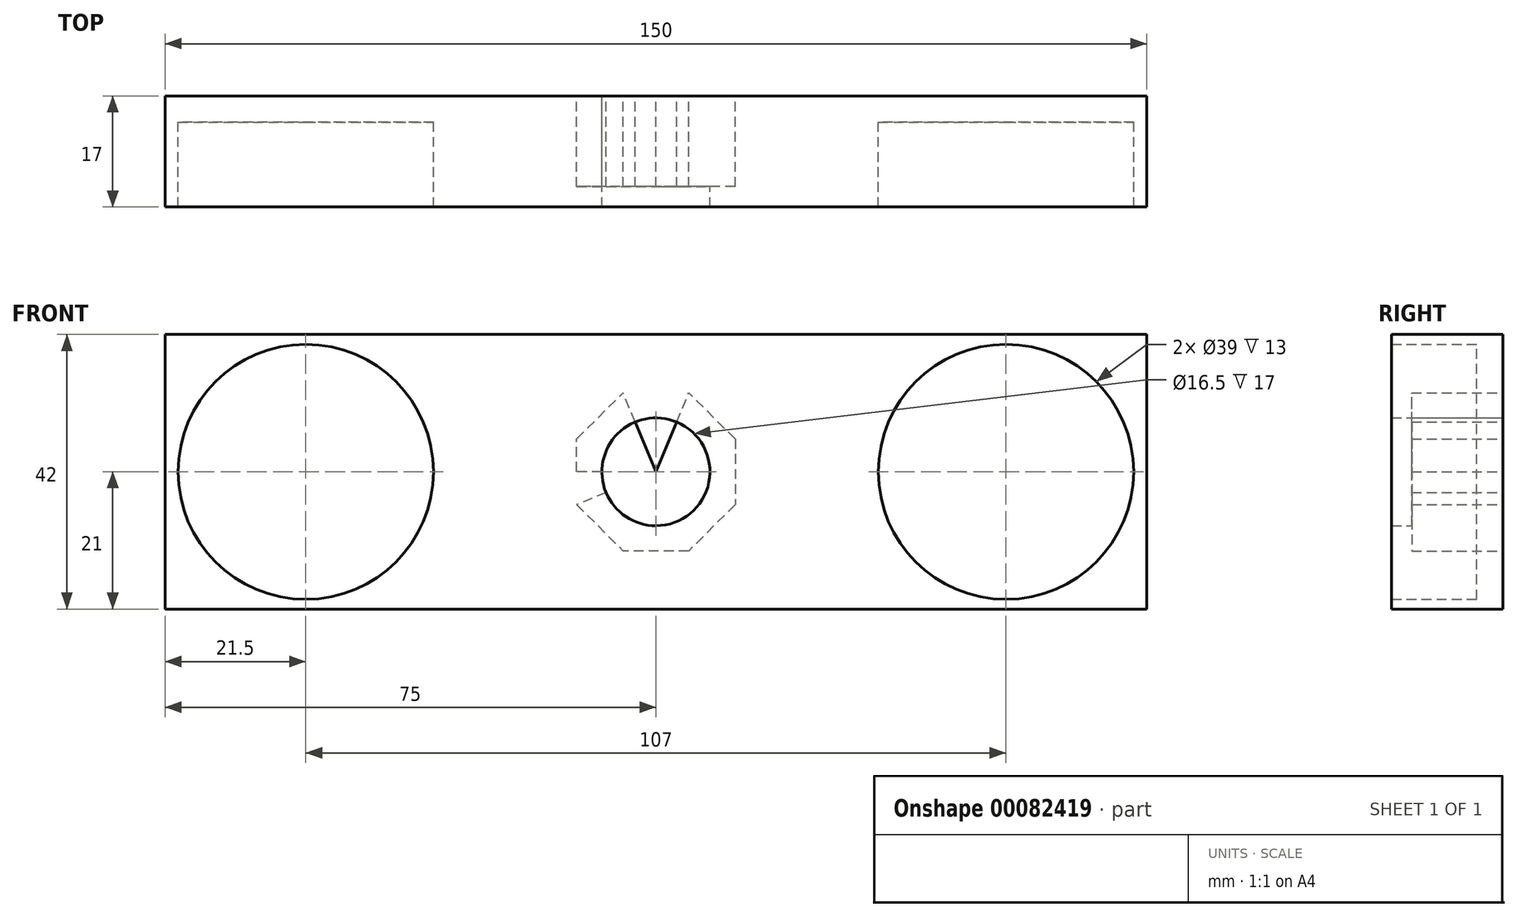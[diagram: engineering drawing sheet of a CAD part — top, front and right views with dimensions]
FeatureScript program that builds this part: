
annotation { "Feature Type Name" : "Feature", "Feature Type Description" : "" }
export const myFeature = defineFeature(function(context is Context, id is Id, definition is map)
    precondition{}
    {
        {
            var Q0;
            Q0=qCreatedBy(makeId("Front.planeOp"),FACE);
            var sketch = newSketch(context, id + "F0", { "sketchPlane" : qUnion([Q0])});
            skLineSegment(sketch, "E0", {"start": v(0, 0) * mm, "end": v(0, 12.1) * mm});
            skLineSegment(sketch, "E1", {"start": v(0, 0) * mm, "end": v(0, -12.1) * mm});
            skLineSegment(sketch, "E2", {"start": v(0, 0) * mm, "end": v(-12.1, 0) * mm});
            skLineSegment(sketch, "E3", {"start": v(0, 0) * mm, "end": v(12.1, 0) * mm});
            skLineSegment(sketch, "E4", {"start": v(0, 12.1) * mm, "end": v(-36.9, 12.1) * mm});
            skLineSegment(sketch, "E5", {"start": v(0, 12.1) * mm, "end": v(53.23, 12.1) * mm});
            skLineSegment(sketch, "E6", {"start": v(0, 0) * mm, "end": v(-5.01, 12.1) * mm});
            skLineSegment(sketch, "E7", {"start": v(0, 0) * mm, "end": v(5.01, 12.1) * mm});
            skLineSegment(sketch, "E8", {"start": v(-5.01, 12.1) * mm, "end": v(5.01, 12.1) * mm});
            skLineSegment(sketch, "E9", {"start": v(-12.1, 0) * mm, "end": v(-12.1, 10.02) * mm});
            skLineSegment(sketch, "E10", {"start": v(-12.1, 0) * mm, "end": v(-12.1, -15.45) * mm});
            skLineSegment(sketch, "E11", {"start": v(0, -12.1) * mm, "end": v(-25.46, -12.1) * mm});
            skLineSegment(sketch, "E12", {"start": v(0, -12.1) * mm, "end": v(28.03, -12.1) * mm});
            skLineSegment(sketch, "E13", {"start": v(12.1, 0) * mm, "end": v(12.1, 12.1) * mm});
            skLineSegment(sketch, "E14", {"start": v(12.1, 0) * mm, "end": v(12.1, -12.1) * mm});
            skLineSegment(sketch, "E15", {"start": v(0, 0) * mm, "end": v(-12.1, 5.01) * mm});
            skLineSegment(sketch, "E16", {"start": v(-12.1, 5.01) * mm, "end": v(-5.01, 12.1) * mm});
            skLineSegment(sketch, "E17", {"start": v(-12.1, 0) * mm, "end": v(-12.1, -5.01) * mm});
            skLineSegment(sketch, "E18", {"start": v(0, 0) * mm, "end": v(-12.1, -5.01) * mm});
            skLineSegment(sketch, "E19", {"start": v(0, 0) * mm, "end": v(-5.01, -12.1) * mm});
            skLineSegment(sketch, "E20", {"start": v(-12.1, -5.01) * mm, "end": v(-5.01, -12.1) * mm});
            skLineSegment(sketch, "E21", {"start": v(0, 0) * mm, "end": v(5.01, -12.1) * mm});
            skLineSegment(sketch, "E22", {"start": v(0, 0) * mm, "end": v(12.1, -5.01) * mm});
            skLineSegment(sketch, "E23", {"start": v(0, 0) * mm, "end": v(12.1, 5.01) * mm});
            skLineSegment(sketch, "E24", {"start": v(12.1, 5.01) * mm, "end": v(5.01, 12.1) * mm});
            skLineSegment(sketch, "E25", {"start": v(12.1, -5.01) * mm, "end": v(5.01, -12.1) * mm});
            skCircle(sketch, "E26", {"center": v(0, 0) * mm, "radius": 8.25 * mm});
            skLineSegment(sketch, "E27", {"start": v(-12.1, 10.02) * mm, "end": v(-12.1, 12.1) * mm});
            skLineSegment(sketch, "E28", {"start": v(-12.1, -5.01) * mm, "end": v(-12.1, -12.1) * mm});
            skSolve(sketch);
        }
        {
            var Q0;
            {var subQ0=sQuery(id+"F0.wireOp",EDGE,"E24");Q0=makeQuery(id+"F0.imprint","IMPRINT",FACE,{"disambiguationData":[TD([[makeQuery(id+"F0.imprint","IMPRINT",EDGE,{"derivedFrom":subQ0}),1.0]])]});}
            var Q1;
            {var subQ0=sQuery(id+"F0.wireOp",EDGE,"E8");var subQ1=sQuery(id+"F0.wireOp",EDGE,"E0");var subQ2=makeQuery(id+"F0.imprint","INTERSECT",VERTEX,{"derivedFrom":[subQ1,subQ0]});Q1=makeQuery(id+"F0.imprint","IMPRINT",FACE,{"disambiguationData":[TD([[makeQuery(id+"F0.imprint","IMPRINT",EDGE,{"disambiguationData":[TD([[subQ2,1.0]])],"derivedFrom":subQ1}),-1.0]])]});}
            var Q2;
            {var subQ0=sQuery(id+"F0.wireOp",EDGE,"E8");var subQ1=sQuery(id+"F0.wireOp",EDGE,"E0");var subQ2=makeQuery(id+"F0.imprint","INTERSECT",VERTEX,{"derivedFrom":[subQ1,subQ0]});Q2=makeQuery(id+"F0.imprint","IMPRINT",FACE,{"disambiguationData":[TD([[makeQuery(id+"F0.imprint","IMPRINT",EDGE,{"disambiguationData":[TD([[subQ2,1.0]])],"derivedFrom":subQ1}),1.0]])]});}
            var Q3;
            {var subQ0=sQuery(id+"F0.wireOp",EDGE,"E16");Q3=makeQuery(id+"F0.imprint","IMPRINT",FACE,{"disambiguationData":[TD([[makeQuery(id+"F0.imprint","IMPRINT",EDGE,{"derivedFrom":subQ0}),-1.0]])]});}
            var Q4;
            {var subQ0=sQuery(id+"F0.wireOp",EDGE,"E20");Q4=makeQuery(id+"F0.imprint","IMPRINT",FACE,{"disambiguationData":[TD([[makeQuery(id+"F0.imprint","IMPRINT",EDGE,{"derivedFrom":subQ0}),1.0]])]});}
            var Q5;
            {var subQ0=sQuery(id+"F0.wireOp",EDGE,"E17");Q5=makeQuery(id+"F0.imprint","IMPRINT",FACE,{"disambiguationData":[TD([[makeQuery(id+"F0.imprint","IMPRINT",EDGE,{"derivedFrom":subQ0}),1.0]])]});}
            var Q6;
            {var subQ1=sQuery(id+"F0.wireOp",EDGE,"E2");var subQ3=sQuery(id+"F0.wireOp",EDGE,"E26");var subQ4=makeQuery(id+"F0.imprint","INTERSECT",VERTEX,{"derivedFrom":[subQ1,subQ3]});Q6=makeQuery(id+"F0.imprint","IMPRINT",FACE,{"disambiguationData":[TD([[makeQuery(id+"F0.imprint","IMPRINT",EDGE,{"disambiguationData":[TD([[subQ4,1.0]])],"derivedFrom":subQ3}),-1.0]])]});}
            var Q7;
            {var subQ1=sQuery(id+"F0.wireOp",EDGE,"E1");var subQ3=sQuery(id+"F0.wireOp",EDGE,"E26");var subQ4=makeQuery(id+"F0.imprint","INTERSECT",VERTEX,{"derivedFrom":[subQ1,subQ3]});Q7=makeQuery(id+"F0.imprint","IMPRINT",FACE,{"disambiguationData":[TD([[makeQuery(id+"F0.imprint","IMPRINT",EDGE,{"disambiguationData":[TD([[subQ4,1.0]])],"derivedFrom":subQ3}),-1.0]])]});}
            var Q8;
            {var subQ1=sQuery(id+"F0.wireOp",EDGE,"E1");var subQ3=sQuery(id+"F0.wireOp",EDGE,"E26");var subQ4=makeQuery(id+"F0.imprint","INTERSECT",VERTEX,{"derivedFrom":[subQ1,subQ3]});Q8=makeQuery(id+"F0.imprint","IMPRINT",FACE,{"disambiguationData":[TD([[makeQuery(id+"F0.imprint","IMPRINT",EDGE,{"disambiguationData":[TD([[subQ4,-1.0]])],"derivedFrom":subQ3}),-1.0]])]});}
            var Q9;
            {var subQ0=sQuery(id+"F0.wireOp",EDGE,"E25");Q9=makeQuery(id+"F0.imprint","IMPRINT",FACE,{"disambiguationData":[TD([[makeQuery(id+"F0.imprint","IMPRINT",EDGE,{"derivedFrom":subQ0}),-1.0]])]});}
            var Q10;
            {var subQ1=sQuery(id+"F0.wireOp",EDGE,"E3");var subQ3=sQuery(id+"F0.wireOp",EDGE,"E26");var subQ4=makeQuery(id+"F0.imprint","INTERSECT",VERTEX,{"derivedFrom":[subQ1,subQ3]});Q10=makeQuery(id+"F0.imprint","IMPRINT",FACE,{"disambiguationData":[TD([[makeQuery(id+"F0.imprint","IMPRINT",EDGE,{"disambiguationData":[TD([[subQ4,1.0]])],"derivedFrom":subQ3}),-1.0]])]});}
            var Q11;
            {var subQ1=sQuery(id+"F0.wireOp",EDGE,"E3");var subQ3=sQuery(id+"F0.wireOp",EDGE,"E26");var subQ4=makeQuery(id+"F0.imprint","INTERSECT",VERTEX,{"derivedFrom":[subQ1,subQ3]});Q11=makeQuery(id+"F0.imprint","IMPRINT",FACE,{"disambiguationData":[TD([[makeQuery(id+"F0.imprint","IMPRINT",EDGE,{"disambiguationData":[TD([[subQ4,-1.0]])],"derivedFrom":subQ3}),-1.0]])]});}
            extrude(context, id + "F1", {"entities" : qUnion([Q0, Q1, Q2, Q3, Q4, Q5, Q6, Q7, Q8, Q9, Q10, Q11]), "depth" : 13.9 * mm});
        }
        {
            var Q0;
            {var subQ1=sQuery(id+"F0.wireOp",EDGE,"E7");var subQ3=sQuery(id+"F0.wireOp",EDGE,"E26");var subQ4=makeQuery(id+"F0.imprint","INTERSECT",VERTEX,{"derivedFrom":[subQ1,subQ3]});Q0=makeQuery(id+"F0.imprint","IMPRINT",FACE,{"disambiguationData":[TD([[makeQuery(id+"F0.imprint","IMPRINT",EDGE,{"disambiguationData":[TD([[subQ4,1.0]])],"derivedFrom":subQ3}),1.0]])]});}
            var Q1;
            {var subQ1=sQuery(id+"F0.wireOp",EDGE,"E0");var subQ3=sQuery(id+"F0.wireOp",EDGE,"E26");var subQ4=makeQuery(id+"F0.imprint","INTERSECT",VERTEX,{"derivedFrom":[subQ1,subQ3]});Q1=makeQuery(id+"F0.imprint","IMPRINT",FACE,{"disambiguationData":[TD([[makeQuery(id+"F0.imprint","IMPRINT",EDGE,{"disambiguationData":[TD([[subQ4,1.0]])],"derivedFrom":subQ3}),1.0]])]});}
            var Q2;
            {var subQ1=sQuery(id+"F0.wireOp",EDGE,"E0");var subQ3=sQuery(id+"F0.wireOp",EDGE,"E26");var subQ4=makeQuery(id+"F0.imprint","INTERSECT",VERTEX,{"derivedFrom":[subQ1,subQ3]});Q2=makeQuery(id+"F0.imprint","IMPRINT",FACE,{"disambiguationData":[TD([[makeQuery(id+"F0.imprint","IMPRINT",EDGE,{"disambiguationData":[TD([[subQ4,-1.0]])],"derivedFrom":subQ3}),1.0]])]});}
            var Q3;
            {var subQ1=sQuery(id+"F0.wireOp",EDGE,"E6");var subQ3=sQuery(id+"F0.wireOp",EDGE,"E26");var subQ4=makeQuery(id+"F0.imprint","INTERSECT",VERTEX,{"derivedFrom":[subQ1,subQ3]});Q3=makeQuery(id+"F0.imprint","IMPRINT",FACE,{"disambiguationData":[TD([[makeQuery(id+"F0.imprint","IMPRINT",EDGE,{"disambiguationData":[TD([[subQ4,-1.0]])],"derivedFrom":subQ3}),1.0]])]});}
            var Q4;
            {var subQ1=sQuery(id+"F0.wireOp",EDGE,"E2");var subQ3=sQuery(id+"F0.wireOp",EDGE,"E26");var subQ4=makeQuery(id+"F0.imprint","INTERSECT",VERTEX,{"derivedFrom":[subQ1,subQ3]});Q4=makeQuery(id+"F0.imprint","IMPRINT",FACE,{"disambiguationData":[TD([[makeQuery(id+"F0.imprint","IMPRINT",EDGE,{"disambiguationData":[TD([[subQ4,1.0]])],"derivedFrom":subQ3}),1.0]])]});}
            var Q5;
            {var subQ1=sQuery(id+"F0.wireOp",EDGE,"E2");var subQ3=sQuery(id+"F0.wireOp",EDGE,"E26");var subQ4=makeQuery(id+"F0.imprint","INTERSECT",VERTEX,{"derivedFrom":[subQ1,subQ3]});Q5=makeQuery(id+"F0.imprint","IMPRINT",FACE,{"disambiguationData":[TD([[makeQuery(id+"F0.imprint","IMPRINT",EDGE,{"disambiguationData":[TD([[subQ4,-1.0]])],"derivedFrom":subQ3}),1.0]])]});}
            var Q6;
            {var subQ1=sQuery(id+"F0.wireOp",EDGE,"E18");var subQ3=sQuery(id+"F0.wireOp",EDGE,"E26");var subQ4=makeQuery(id+"F0.imprint","INTERSECT",VERTEX,{"derivedFrom":[subQ1,subQ3]});Q6=makeQuery(id+"F0.imprint","IMPRINT",FACE,{"disambiguationData":[TD([[makeQuery(id+"F0.imprint","IMPRINT",EDGE,{"disambiguationData":[TD([[subQ4,-1.0]])],"derivedFrom":subQ3}),1.0]])]});}
            var Q7;
            {var subQ1=sQuery(id+"F0.wireOp",EDGE,"E1");var subQ3=sQuery(id+"F0.wireOp",EDGE,"E26");var subQ4=makeQuery(id+"F0.imprint","INTERSECT",VERTEX,{"derivedFrom":[subQ1,subQ3]});Q7=makeQuery(id+"F0.imprint","IMPRINT",FACE,{"disambiguationData":[TD([[makeQuery(id+"F0.imprint","IMPRINT",EDGE,{"disambiguationData":[TD([[subQ4,1.0]])],"derivedFrom":subQ3}),1.0]])]});}
            var Q8;
            {var subQ1=sQuery(id+"F0.wireOp",EDGE,"E1");var subQ3=sQuery(id+"F0.wireOp",EDGE,"E26");var subQ4=makeQuery(id+"F0.imprint","INTERSECT",VERTEX,{"derivedFrom":[subQ1,subQ3]});Q8=makeQuery(id+"F0.imprint","IMPRINT",FACE,{"disambiguationData":[TD([[makeQuery(id+"F0.imprint","IMPRINT",EDGE,{"disambiguationData":[TD([[subQ4,-1.0]])],"derivedFrom":subQ3}),1.0]])]});}
            var Q9;
            {var subQ1=sQuery(id+"F0.wireOp",EDGE,"E21");var subQ3=sQuery(id+"F0.wireOp",EDGE,"E26");var subQ4=makeQuery(id+"F0.imprint","INTERSECT",VERTEX,{"derivedFrom":[subQ1,subQ3]});Q9=makeQuery(id+"F0.imprint","IMPRINT",FACE,{"disambiguationData":[TD([[makeQuery(id+"F0.imprint","IMPRINT",EDGE,{"disambiguationData":[TD([[subQ4,-1.0]])],"derivedFrom":subQ3}),1.0]])]});}
            var Q10;
            {var subQ1=sQuery(id+"F0.wireOp",EDGE,"E3");var subQ3=sQuery(id+"F0.wireOp",EDGE,"E26");var subQ4=makeQuery(id+"F0.imprint","INTERSECT",VERTEX,{"derivedFrom":[subQ1,subQ3]});Q10=makeQuery(id+"F0.imprint","IMPRINT",FACE,{"disambiguationData":[TD([[makeQuery(id+"F0.imprint","IMPRINT",EDGE,{"disambiguationData":[TD([[subQ4,1.0]])],"derivedFrom":subQ3}),1.0]])]});}
            var Q11;
            {var subQ1=sQuery(id+"F0.wireOp",EDGE,"E3");var subQ3=sQuery(id+"F0.wireOp",EDGE,"E26");var subQ4=makeQuery(id+"F0.imprint","INTERSECT",VERTEX,{"derivedFrom":[subQ1,subQ3]});Q11=makeQuery(id+"F0.imprint","IMPRINT",FACE,{"disambiguationData":[TD([[makeQuery(id+"F0.imprint","IMPRINT",EDGE,{"disambiguationData":[TD([[subQ4,-1.0]])],"derivedFrom":subQ3}),1.0]])]});}
            extrude(context, id + "F2", {"entities" : qUnion([Q0, Q1, Q2, Q3, Q4, Q5, Q6, Q7, Q8, Q9, Q10, Q11]), "depth" : 25 * mm});
        }
        {
            var Q0;
            Q0=qCreatedBy(makeId("Front.planeOp"),FACE);
            var sketch = newSketch(context, id + "F3", { "sketchPlane" : qUnion([Q0])});
            skLineSegment(sketch, "E29.bottom", {"start": v(-75, 21) * mm, "end": v(75, 21) * mm});
            skLineSegment(sketch, "E29.top", {"start": v(-75, -21) * mm, "end": v(75, -21) * mm});
            skLineSegment(sketch, "E29.left", {"start": v(-75, 21) * mm, "end": v(-75, -21) * mm});
            skLineSegment(sketch, "E29.right", {"start": v(75, 21) * mm, "end": v(75, -21) * mm});
            skPoint(sketch, "E29.middle", {"position": v(0, 0) * mm});
            skCircle(sketch, "E30", {"center": v(-53.5, 0) * mm, "radius": 19.5 * mm});
            skLineSegment(sketch, "E31", {"start": v(-75, 0) * mm, "end": v(-73, 0) * mm});
            skCircle(sketch, "E32", {"center": v(53.5, 0) * mm, "radius": 19.5 * mm});
            skLineSegment(sketch, "E33", {"start": v(73, 0) * mm, "end": v(75, 0) * mm});
            skSolve(sketch);
        }
        {
            var Q0;
            Q0=makeQuery(id+"F3.imprint","IMPRINT",FACE,{"disambiguationData":[TD([[makeQuery(id+"F3.imprint","IMPRINT",EDGE,{"derivedFrom":sQuery(id+"F3.wireOp",EDGE,"E29.bottom")}),-1.0]])]});
            var Q1;
            Q1=makeQuery(id+"F3.imprint","IMPRINT",FACE,{"disambiguationData":[TD([[makeQuery(id+"F3.imprint","IMPRINT",EDGE,{"derivedFrom":sQuery(id+"F3.wireOp",EDGE,"E30")}),1.0]])]});
            var Q2;
            Q2=makeQuery(id+"F3.imprint","IMPRINT",FACE,{"disambiguationData":[TD([[makeQuery(id+"F3.imprint","IMPRINT",EDGE,{"derivedFrom":sQuery(id+"F3.wireOp",EDGE,"E32")}),1.0]])]});
            extrude(context, id + "F4", {"entities" : qUnion([Q0, Q1, Q2]), "depth" : 17 * mm});
        }
        {
            var Q0;
            Q0=makeQuery(id+"F2.opExtrude","SWEPT_BODY",BODY,{"disambiguationData":[OSD([sQuery(id+"F0.wireOp",EDGE,"E26")])]});
            var Q1;
            Q1=makeQuery(id+"F1.opExtrude","SWEPT_BODY",BODY,{"disambiguationData":[OSD([sQuery(id+"F0.wireOp",EDGE,"E8"),sQuery(id+"F0.wireOp",EDGE,"E9"),sQuery(id+"F0.wireOp",EDGE,"E11"),sQuery(id+"F0.wireOp",EDGE,"E12"),sQuery(id+"F0.wireOp",EDGE,"E13"),sQuery(id+"F0.wireOp",EDGE,"E14"),sQuery(id+"F0.wireOp",EDGE,"E16"),sQuery(id+"F0.wireOp",EDGE,"E17"),sQuery(id+"F0.wireOp",EDGE,"E20"),sQuery(id+"F0.wireOp",EDGE,"E24"),sQuery(id+"F0.wireOp",EDGE,"E25"),sQuery(id+"F0.wireOp",EDGE,"E26")])]});
            var Q2;
            Q2=makeQuery(id+"F4.opExtrude","SWEPT_BODY",BODY,{"disambiguationData":[OSD([sQuery(id+"F3.wireOp",EDGE,"E29.bottom"),sQuery(id+"F3.wireOp",EDGE,"E29.top"),sQuery(id+"F3.wireOp",EDGE,"E29.left"),sQuery(id+"F3.wireOp",EDGE,"E29.right")])]});
            booleanBodies(context, id + "F5", {"operationType" : BooleanOperationType.SUBTRACTION, "tools" : qUnion([Q0, Q1]), "targets" : qUnion([Q2])});
        }
        {
            var Q0;
            Q0=makeQuery(id+"F3.imprint","IMPRINT",FACE,{"disambiguationData":[TD([[makeQuery(id+"F3.imprint","IMPRINT",EDGE,{"derivedFrom":sQuery(id+"F3.wireOp",EDGE,"E30")}),1.0]])]});
            var Q1;
            Q1=makeQuery(id+"F3.imprint","IMPRINT",FACE,{"disambiguationData":[TD([[makeQuery(id+"F3.imprint","IMPRINT",EDGE,{"derivedFrom":sQuery(id+"F3.wireOp",EDGE,"E32")}),1.0]])]});
            extrude(context, id + "F6", {"entities" : qUnion([Q0, Q1]), "depth" : 20.74 * mm});
        }
        {
            var Q0;
            Q0=makeQuery(id+"F6.opExtrude","SWEPT_BODY",BODY,{"disambiguationData":[OSD([sQuery(id+"F3.wireOp",EDGE,"E30")])]});
            var Q1;
            Q1=makeQuery(id+"F6.opExtrude","SWEPT_BODY",BODY,{"disambiguationData":[OSD([sQuery(id+"F3.wireOp",EDGE,"E32")])]});
            transform(context, id + "F7", {"entities" : qUnion([Q0, Q1]), "transformType" : TransformType.TRANSLATION_3D, "dx" : 0 * mm, "dy" : -4 * mm, "dz" : 0 * mm, "makeCopy" : false});
        }
        {
            var Q0;
            Q0=makeQuery(id+"F6.opExtrude","SWEPT_BODY",BODY,{"disambiguationData":[OSD([sQuery(id+"F3.wireOp",EDGE,"E30")])]});
            var Q1;
            Q1=makeQuery(id+"F6.opExtrude","SWEPT_BODY",BODY,{"disambiguationData":[OSD([sQuery(id+"F3.wireOp",EDGE,"E32")])]});
            var Q2;
            Q2=makeQuery(id+"F4.opExtrude","SWEPT_BODY",BODY,{"disambiguationData":[OSD([sQuery(id+"F3.wireOp",EDGE,"E29.bottom"),sQuery(id+"F3.wireOp",EDGE,"E29.top"),sQuery(id+"F3.wireOp",EDGE,"E29.left"),sQuery(id+"F3.wireOp",EDGE,"E29.right"),sQuery(id+"F3.wireOp",EDGE,"E30"),sQuery(id+"F3.wireOp",EDGE,"E32")])]});
            booleanBodies(context, id + "F8", {"operationType" : BooleanOperationType.SUBTRACTION, "tools" : qUnion([Q0, Q1]), "targets" : qUnion([Q2])});
        }
    });
